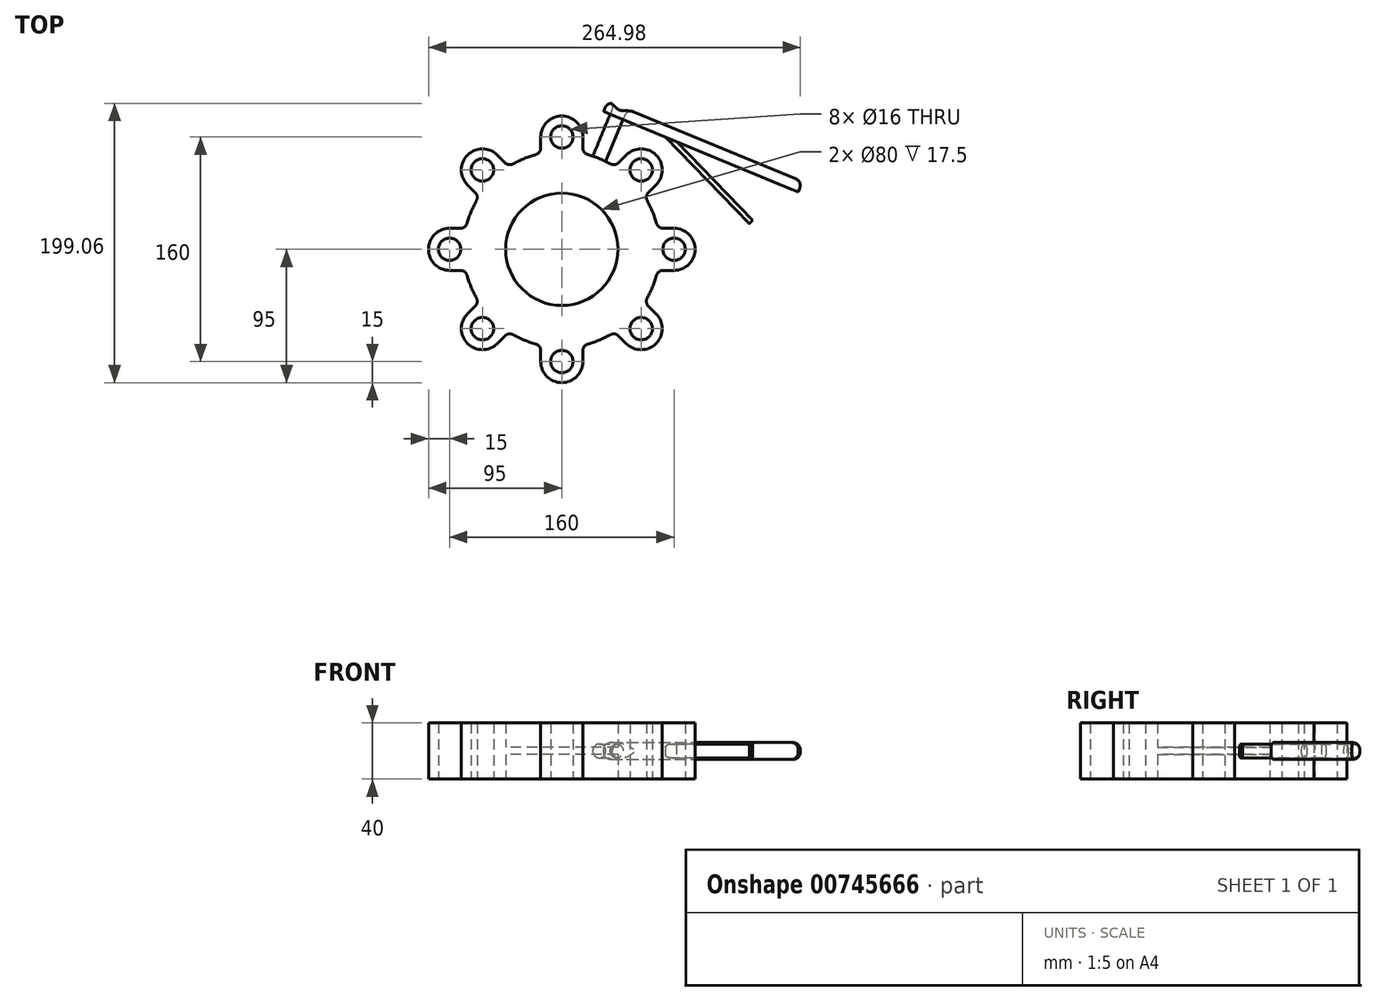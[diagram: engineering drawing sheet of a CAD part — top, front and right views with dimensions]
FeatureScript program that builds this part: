
annotation { "Feature Type Name" : "Feature", "Feature Type Description" : "" }
export const myFeature = defineFeature(function(context is Context, id is Id, definition is map)
    precondition{}
    {
        {
            var Q0;
            Q0=qCreatedBy(makeId("Top.planeOp"),FACE);
            var sketch = newSketch(context, id + "F0", { "sketchPlane" : qUnion([Q0])});
            skCircle(sketch, "E0", {"center": v(0, 0) * mm, "radius": 40 * mm});
            skArc(sketch, "E1", {"start": v(-18.67, 67.47) * mm, "mid": v(0, -70) * mm, "end": v(18.67, 67.47) * mm});
            skCircle(sketch, "E2", {"center": v(0, 80) * mm, "radius": 8 * mm});
            skCircle(sketch, "E3.1.0", {"center": v(-56.57, 56.57) * mm, "radius": 8 * mm});
            skCircle(sketch, "E3.2.0", {"center": v(-80, 0) * mm, "radius": 8 * mm});
            skCircle(sketch, "E3.3.0", {"center": v(-56.57, -56.57) * mm, "radius": 8 * mm});
            skCircle(sketch, "E3.4.0", {"center": v(0, -80) * mm, "radius": 8 * mm});
            skCircle(sketch, "E3.5.0", {"center": v(56.57, -56.57) * mm, "radius": 8 * mm});
            skCircle(sketch, "E3.6.0", {"center": v(80, 0) * mm, "radius": 8 * mm});
            skCircle(sketch, "E3.7.0", {"center": v(56.57, 56.57) * mm, "radius": 8 * mm});
            skArc(sketch, "E4", {"start": v(15, 80) * mm, "mid": v(0, 95) * mm, "end": v(-15, 80) * mm});
            skLineSegment(sketch, "E5", {"start": v(15, 80) * mm, "end": v(15, 72.28) * mm});
            skLineSegment(sketch, "E6", {"start": v(-15, 80) * mm, "end": v(-15, 72.28) * mm});
            skPoint(sketch, "E7.visualSharp", {"position": v(-15, 68.37) * mm});
            skArc(sketch, "E7.filletArc", {"start": v(-18.67, 67.47) * mm, "mid": v(-16.02, 69.26) * mm, "end": v(-15, 72.28) * mm});
            skPoint(sketch, "E8.visualSharp", {"position": v(15, 68.37) * mm});
            skArc(sketch, "E8.filletArc", {"start": v(15, 72.28) * mm, "mid": v(16.02, 69.26) * mm, "end": v(18.67, 67.47) * mm});
            skArc(sketch, "E9.1.0", {"start": v(-45.96, 67.18) * mm, "mid": v(-67.18, 67.18) * mm, "end": v(-67.18, 45.96) * mm});
            skLineSegment(sketch, "E9.1.1", {"start": v(-67.18, 45.96) * mm, "end": v(-61.72, 40.5) * mm});
            skArc(sketch, "E9.1.2", {"start": v(-60.9, 34.5) * mm, "mid": v(-60.3, 37.64) * mm, "end": v(-61.72, 40.5) * mm});
            skLineSegment(sketch, "E9.1.3", {"start": v(-45.96, 67.18) * mm, "end": v(-40.5, 61.72) * mm});
            skArc(sketch, "E9.1.4", {"start": v(-40.5, 61.72) * mm, "mid": v(-37.64, 60.3) * mm, "end": v(-34.5, 60.9) * mm});
            skArc(sketch, "E9.2.0", {"start": v(-80, 15) * mm, "mid": v(-95, 0) * mm, "end": v(-80, -15) * mm});
            skLineSegment(sketch, "E9.2.1", {"start": v(-80, -15) * mm, "end": v(-72.28, -15) * mm});
            skArc(sketch, "E9.2.2", {"start": v(-67.47, -18.67) * mm, "mid": v(-69.26, -16.02) * mm, "end": v(-72.28, -15) * mm});
            skLineSegment(sketch, "E9.2.3", {"start": v(-80, 15) * mm, "end": v(-72.28, 15) * mm});
            skArc(sketch, "E9.2.4", {"start": v(-72.28, 15) * mm, "mid": v(-69.26, 16.02) * mm, "end": v(-67.47, 18.67) * mm});
            skArc(sketch, "E9.3.0", {"start": v(-67.18, -45.96) * mm, "mid": v(-67.18, -67.18) * mm, "end": v(-45.96, -67.18) * mm});
            skLineSegment(sketch, "E9.3.1", {"start": v(-45.96, -67.18) * mm, "end": v(-40.5, -61.72) * mm});
            skArc(sketch, "E9.3.2", {"start": v(-34.5, -60.9) * mm, "mid": v(-37.64, -60.3) * mm, "end": v(-40.5, -61.72) * mm});
            skLineSegment(sketch, "E9.3.3", {"start": v(-67.18, -45.96) * mm, "end": v(-61.72, -40.5) * mm});
            skArc(sketch, "E9.3.4", {"start": v(-61.72, -40.5) * mm, "mid": v(-60.3, -37.64) * mm, "end": v(-60.9, -34.5) * mm});
            skArc(sketch, "E9.4.0", {"start": v(-15, -80) * mm, "mid": v(0, -95) * mm, "end": v(15, -80) * mm});
            skLineSegment(sketch, "E9.4.1", {"start": v(15, -80) * mm, "end": v(15, -72.28) * mm});
            skArc(sketch, "E9.4.2", {"start": v(18.67, -67.47) * mm, "mid": v(16.02, -69.26) * mm, "end": v(15, -72.28) * mm});
            skLineSegment(sketch, "E9.4.3", {"start": v(-15, -80) * mm, "end": v(-15, -72.28) * mm});
            skArc(sketch, "E9.4.4", {"start": v(-15, -72.28) * mm, "mid": v(-16.02, -69.26) * mm, "end": v(-18.67, -67.47) * mm});
            skArc(sketch, "E9.5.0", {"start": v(45.96, -67.18) * mm, "mid": v(67.18, -67.18) * mm, "end": v(67.18, -45.96) * mm});
            skLineSegment(sketch, "E9.5.1", {"start": v(67.18, -45.96) * mm, "end": v(61.72, -40.5) * mm});
            skArc(sketch, "E9.5.2", {"start": v(60.9, -34.5) * mm, "mid": v(60.3, -37.64) * mm, "end": v(61.72, -40.5) * mm});
            skLineSegment(sketch, "E9.5.3", {"start": v(45.96, -67.18) * mm, "end": v(40.5, -61.72) * mm});
            skArc(sketch, "E9.5.4", {"start": v(40.5, -61.72) * mm, "mid": v(37.64, -60.3) * mm, "end": v(34.5, -60.9) * mm});
            skArc(sketch, "E9.6.0", {"start": v(80, -15) * mm, "mid": v(95, 0) * mm, "end": v(80, 15) * mm});
            skLineSegment(sketch, "E9.6.1", {"start": v(80, 15) * mm, "end": v(72.28, 15) * mm});
            skArc(sketch, "E9.6.2", {"start": v(67.47, 18.67) * mm, "mid": v(69.26, 16.02) * mm, "end": v(72.28, 15) * mm});
            skLineSegment(sketch, "E9.6.3", {"start": v(80, -15) * mm, "end": v(72.28, -15) * mm});
            skArc(sketch, "E9.6.4", {"start": v(72.28, -15) * mm, "mid": v(69.26, -16.02) * mm, "end": v(67.47, -18.67) * mm});
            skArc(sketch, "E9.7.0", {"start": v(67.18, 45.96) * mm, "mid": v(67.18, 67.18) * mm, "end": v(45.96, 67.18) * mm});
            skLineSegment(sketch, "E9.7.1", {"start": v(45.96, 67.18) * mm, "end": v(40.5, 61.72) * mm});
            skArc(sketch, "E9.7.2", {"start": v(34.5, 60.9) * mm, "mid": v(37.64, 60.3) * mm, "end": v(40.5, 61.72) * mm});
            skLineSegment(sketch, "E9.7.3", {"start": v(67.18, 45.96) * mm, "end": v(61.72, 40.5) * mm});
            skArc(sketch, "E9.7.4", {"start": v(61.72, 40.5) * mm, "mid": v(60.3, 37.64) * mm, "end": v(60.9, 34.5) * mm});
            skSolve(sketch);
        }
        {
            var Q0;
            Q0 = qSketchRegion(id + "F0", true);
            extrude(context, id + "F1", {"entities" : qUnion([Q0]), "endBound" : BoundingType.SYMMETRIC, "depth" : 40 * mm, "offsetDistance" : 25 * mm});
        }
        {
            var Q0;
            Q0=qCreatedBy(makeId("Top.planeOp"),FACE);
            var sketch = newSketch(context, id + "F2", { "sketchPlane" : qUnion([Q0])});
            skLineSegment(sketch, "E10", {"start": v(34.49, 96.33) * mm, "end": v(16.61, 53.17) * mm});
            skLineSegment(sketch, "E11", {"start": v(43.73, 92.5) * mm, "end": v(25.85, 49.35) * mm});
            skLineSegment(sketch, "E12", {"start": v(34.49, 96.33) * mm, "end": v(43.73, 92.5) * mm});
            skLineSegment(sketch, "E13", {"start": v(16.61, 53.17) * mm, "end": v(25.85, 49.35) * mm});
            skSolve(sketch);
        }
        {
            var Q0;
            Q0=makeQuery(id+"F2.imprint","IMPRINT",FACE,{"disambiguationData":[TD([[makeQuery(id+"F2.imprint","IMPRINT",EDGE,{"derivedFrom":sQuery(id+"F2.wireOp",EDGE,"E10")}),1.0]])]});
            extrude(context, id + "F3", {"entities" : qUnion([Q0]), "operationType" : NewBodyOperationType.ADD, "endBound" : BoundingType.SYMMETRIC, "depth" : 10 * mm, "offsetDistance" : 25 * mm});
        }
        {
            var Q0;
            Q0=makeQuery(id+"F3.opExtrude","CAP_EDGE",EDGE,{"disambiguationData":[OSD([sQuery(id+"F2.wireOp",EDGE,"E11")])],"isStart":false});
            var Q1;
            Q1=makeQuery(id+"F3.opExtrude","CAP_EDGE",EDGE,{"disambiguationData":[OSD([sQuery(id+"F2.wireOp",EDGE,"E10")])],"isStart":false});
            var Q2;
            Q2=makeQuery(id+"F3.opExtrude","CAP_EDGE",EDGE,{"disambiguationData":[OSD([sQuery(id+"F2.wireOp",EDGE,"E10")])],"isStart":true});
            var Q3;
            Q3=makeQuery(id+"F3.opExtrude","CAP_EDGE",EDGE,{"disambiguationData":[OSD([sQuery(id+"F2.wireOp",EDGE,"E11")])],"isStart":true});
            fillet(context, id + "F4", {"entities" : qUnion([Q0, Q1, Q2, Q3]), "radius" : 5 * mm, "tangentPropagation" : true, "allowEdgeOverflow" : false});
        }
        {
            var Q0;
            Q0=makeQuery(id+"F3.opExtrude","SWEPT_FACE",FACE,{"disambiguationData":[OSD([sQuery(id+"F2.wireOp",EDGE,"E12")])]});
            var sketch = newSketch(context, id + "F5", { "sketchPlane" : qUnion([Q0])});
            skLineSegment(sketch, "E14.bottom", {"start": v(10, -6) * mm, "end": v(-140, -6) * mm});
            skLineSegment(sketch, "E14.top", {"start": v(10, 6) * mm, "end": v(-140, 6) * mm});
            skLineSegment(sketch, "E14.left", {"start": v(10, -6) * mm, "end": v(10, 6) * mm});
            skLineSegment(sketch, "E14.right", {"start": v(-140, -6) * mm, "end": v(-140, 6) * mm});
            skSolve(sketch);
        }
        {
            var Q0;
            Q0=makeQuery(id+"F5.imprint","IMPRINT",FACE,{"disambiguationData":[TD([[makeQuery(id+"F5.imprint","IMPRINT",EDGE,{"derivedFrom":sQuery(id+"F5.wireOp",EDGE,"E14.bottom")}),-1.0]])]});
            var Q1;
            Q1=makeQuery(id+"F5.imprint","IMPRINT",FACE,{"disambiguationData":[TD([[makeQuery(id+"F5.imprint","IMPRINT",EDGE,{"derivedFrom":makeQuery(id+"F4.opFillet","BLEND_EDGE",EDGE,{"blendedFrom":[makeQuery(id+"F3.opExtrude","CAP_EDGE",EDGE,{"disambiguationData":[OSD([sQuery(id+"F2.wireOp",EDGE,"E11")])],"isStart":false}),makeQuery(id+"F3.opExtrude","SWEPT_FACE",FACE,{"disambiguationData":[OSD([sQuery(id+"F2.wireOp",EDGE,"E12")])]})],"blendedInto":[makeQuery(id+"F3.opExtrude","SWEPT_FACE",FACE,{"disambiguationData":[OSD([sQuery(id+"F2.wireOp",EDGE,"E12")])]})]})}),1.0]])]});
            extrude(context, id + "F6", {"entities" : qUnion([Q0, Q1]), "operationType" : NewBodyOperationType.ADD, "depth" : 8 * mm, "offsetDistance" : 25 * mm});
        }
        {
            var Q0;
            Q0=makeQuery(id+"F6.opExtrude","SWEPT_EDGE",EDGE,{"disambiguationData":[OSD([sQuery(id+"F5.wireOp",EDGE,"E14.top"),sQuery(id+"F5.wireOp",EDGE,"E14.left")])]});
            var Q1;
            Q1=makeQuery(id+"F6.opExtrude","SWEPT_EDGE",EDGE,{"disambiguationData":[OSD([sQuery(id+"F5.wireOp",EDGE,"E14.bottom"),sQuery(id+"F5.wireOp",EDGE,"E14.left")])]});
            var Q2;
            Q2=makeQuery(id+"F6.opExtrude","CAP_EDGE",EDGE,{"disambiguationData":[OSD([sQuery(id+"F5.wireOp",EDGE,"E14.top")])],"isStart":false});
            var Q3;
            Q3=makeQuery(id+"F6.opExtrude","CAP_FACE",FACE,{"disambiguationData":[OSD([sQuery(id+"F5.wireOp",EDGE,"E14.bottom"),sQuery(id+"F5.wireOp",EDGE,"E14.top"),sQuery(id+"F5.wireOp",EDGE,"E14.left"),sQuery(id+"F5.wireOp",EDGE,"E14.right")])],"isStart":false});
            var Q4;
            Q4=makeQuery(id+"F6.opExtrude","SWEPT_EDGE",EDGE,{"disambiguationData":[OSD([sQuery(id+"F5.wireOp",EDGE,"E14.top"),sQuery(id+"F5.wireOp",EDGE,"E14.right")])]});
            var Q5;
            Q5=makeQuery(id+"F6.opExtrude","SWEPT_EDGE",EDGE,{"disambiguationData":[OSD([sQuery(id+"F5.wireOp",EDGE,"E14.bottom"),sQuery(id+"F5.wireOp",EDGE,"E14.right")])]});
            fillet(context, id + "F7", {"entities" : qUnion([Q0, Q1, Q2, Q3, Q4, Q5]), "radius" : 5 * mm, "tangentPropagation" : true, "allowEdgeOverflow" : false});
        }
        {
            var Q0;
            Q0=qCreatedBy(makeId("Top.planeOp"),FACE);
            var sketch = newSketch(context, id + "F8", { "sketchPlane" : qUnion([Q0])});
            skLineSegment(sketch, "E15.0", {"start": v(34.49, 96.33) * mm, "end": v(163.83, 42.76) * mm});
            skLineSegment(sketch, "E16", {"start": v(81.54, 76.84) * mm, "end": v(136.01, 20.63) * mm});
            skLineSegment(sketch, "E17", {"start": v(136.01, 20.63) * mm, "end": v(133.65, 18.34) * mm});
            skLineSegment(sketch, "E18", {"start": v(133.65, 18.34) * mm, "end": v(73.87, 80.02) * mm});
            skSolve(sketch);
        }
        {
            var Q0;
            {var subQ0=sQuery(id+"F8.wireOp",EDGE,"E16");Q0=makeQuery(id+"F8.imprint","IMPRINT",FACE,{"disambiguationData":[TD([[makeQuery(id+"F8.imprint","IMPRINT",EDGE,{"derivedFrom":subQ0}),-1.0]])]});}
            extrude(context, id + "F9", {"entities" : qUnion([Q0]), "operationType" : NewBodyOperationType.ADD, "endBound" : BoundingType.SYMMETRIC, "depth" : 10 * mm, "offsetDistance" : 25 * mm});
        }
        {
            var Q0;
            Q0=makeQuery(id+"F9.opExtrude","CAP_EDGE",EDGE,{"disambiguationData":[OSD([sQuery(id+"F8.wireOp",EDGE,"E18")])],"isStart":false});
            var Q1;
            Q1=makeQuery(id+"F9.opExtrude","CAP_EDGE",EDGE,{"disambiguationData":[OSD([sQuery(id+"F8.wireOp",EDGE,"E18")])],"isStart":true});
            fillet(context, id + "F10", {"entities" : qUnion([Q0, Q1]), "radius" : 2 * mm, "tangentPropagation" : true, "allowEdgeOverflow" : false});
        }
        {
            var Q0;
            Q0=qCreatedBy(makeId("Top.planeOp"),FACE);
            var sketch = newSketch(context, id + "F11", { "sketchPlane" : qUnion([Q0])});
            skCircle(sketch, "E19.0", {"center": v(0, 0) * mm, "radius": 40 * mm});
            skSolve(sketch);
        }
        {
            var Q0;
            Q0=makeQuery(id+"F11.imprint","IMPRINT",FACE,{"disambiguationData":[TD([[makeQuery(id+"F11.imprint","IMPRINT",EDGE,{"derivedFrom":sQuery(id+"F11.wireOp",EDGE,"E19.0")}),1.0]])]});
            extrude(context, id + "F12", {"entities" : qUnion([Q0]), "operationType" : NewBodyOperationType.ADD, "endBound" : BoundingType.SYMMETRIC, "depth" : 5 * mm, "offsetDistance" : 25 * mm});
        }
    });
